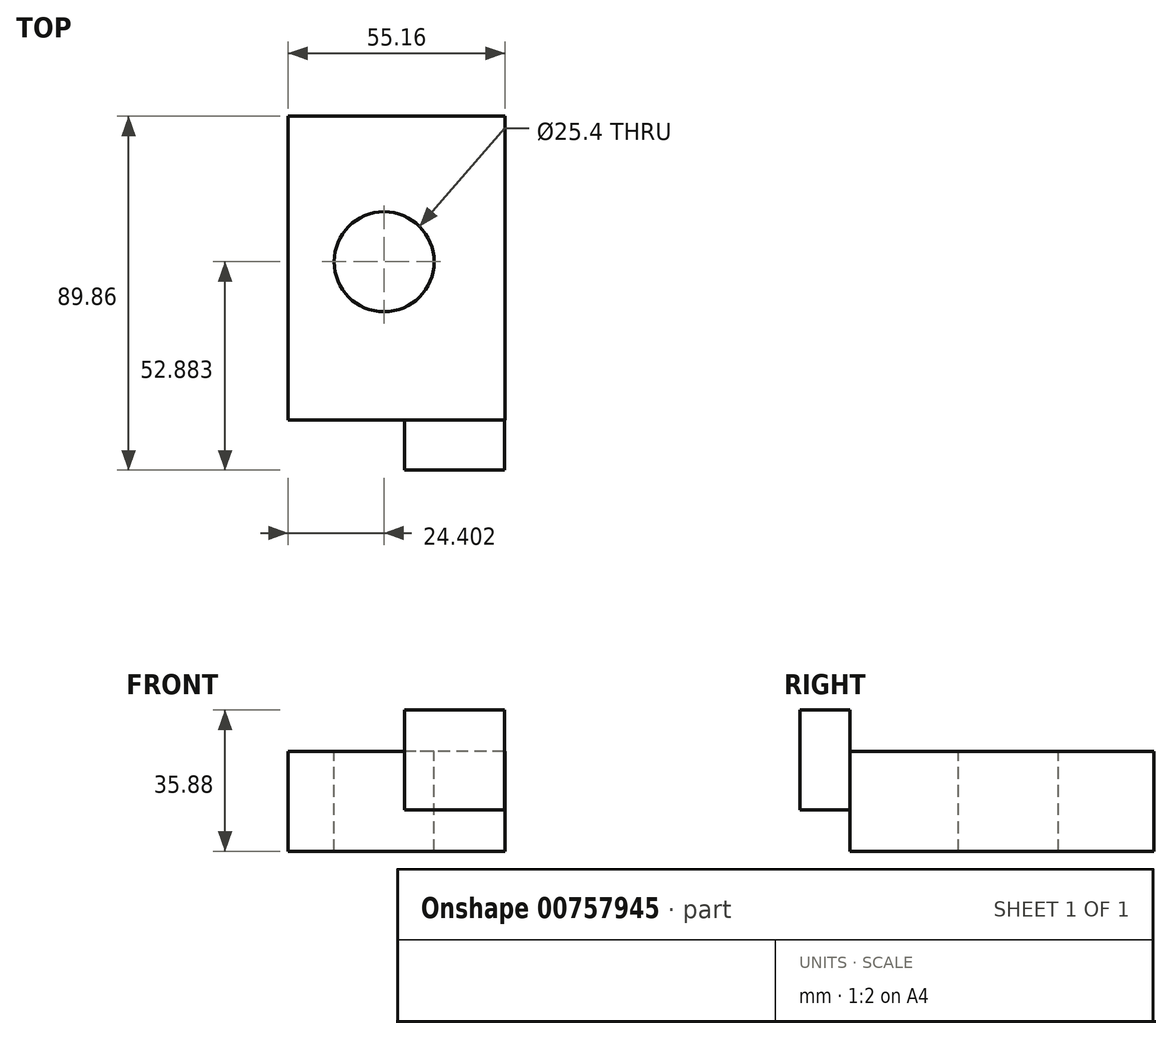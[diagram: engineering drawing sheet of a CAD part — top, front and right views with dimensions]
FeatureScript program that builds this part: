
annotation { "Feature Type Name" : "Feature", "Feature Type Description" : "" }
export const myFeature = defineFeature(function(context is Context, id is Id, definition is map)
    precondition{}
    {
        {
            var Q0;
            Q0=qCreatedBy(makeId("Top.planeOp"),FACE);
            var sketch = newSketch(context, id + "F0", { "sketchPlane" : qUnion([Q0])});
            skLineSegment(sketch, "E0.bottom", {"start": v(0, 0) * mm, "end": v(-55.16, 0) * mm});
            skLineSegment(sketch, "E0.top", {"start": v(0, 77.16) * mm, "end": v(-55.16, 77.16) * mm});
            skLineSegment(sketch, "E0.left", {"start": v(0, 0) * mm, "end": v(0, 77.16) * mm});
            skLineSegment(sketch, "E0.right", {"start": v(-55.16, 0) * mm, "end": v(-55.16, 77.16) * mm});
            skSolve(sketch);
        }
        {
            var Q0;
            Q0=makeQuery(id+"F0.imprint","IMPRINT",FACE,{"disambiguationData":[TD([[makeQuery(id+"F0.imprint","IMPRINT",EDGE,{"derivedFrom":sQuery(id+"F0.wireOp",EDGE,"E0.bottom")}),-1.0]])]});
            extrude(context, id + "F1", {"entities" : qUnion([Q0]), "depth" : 25.4 * mm, "offsetDistance" : 25.4 * mm});
        }
        {
            var Q0;
            Q0=makeQuery(id+"F1.opExtrude","CAP_FACE",FACE,{"disambiguationData":[OSD([sQuery(id+"F0.wireOp",EDGE,"E0.bottom"),sQuery(id+"F0.wireOp",EDGE,"E0.top"),sQuery(id+"F0.wireOp",EDGE,"E0.left"),sQuery(id+"F0.wireOp",EDGE,"E0.right")])],"isStart":false});
            var sketch = newSketch(context, id + "F2", { "sketchPlane" : qUnion([Q0])});
            skPoint(sketch, "E1", {"position": v(-30.76, 40.18) * mm});
            skSolve(sketch);
        }
        {
            var Q0;
            Q0=sQuery(id+"F2.wireOp",VERTEX,"E1");
            var Q1;
            Q1=makeQuery(id+"F1.opExtrude","SWEPT_BODY",BODY,{"disambiguationData":[OSD([sQuery(id+"F0.wireOp",EDGE,"E0.bottom"),sQuery(id+"F0.wireOp",EDGE,"E0.top"),sQuery(id+"F0.wireOp",EDGE,"E0.left"),sQuery(id+"F0.wireOp",EDGE,"E0.right")])]});
            hole(context, id + "F3", {"style" : HoleStyle.SIMPLE, "endStyle" : HoleEndStyle.THROUGH, "holeDiameter" : 25.4 * mm, "majorDiameter" : 6.35 * mm, "isTappedThrough" : true, "tappedDepth" : 12.7 * mm, "tapClearance" : 3, "locations" : qUnion([Q0]), "scope" : qUnion([Q1])});
        }
        {
            var Q0;
            Q0=makeQuery(id+"F1.opExtrude","SWEPT_FACE",FACE,{"disambiguationData":[OSD([sQuery(id+"F0.wireOp",EDGE,"E0.bottom")])]});
            var sketch = newSketch(context, id + "F4", { "sketchPlane" : qUnion([Q0])});
            skPoint(sketch, "E2", {"position": v(-17.06, 38.1) * mm});
            skPoint(sketch, "E3", {"position": v(-75.74, 38.1) * mm});
            skLineSegment(sketch, "E4.bottom", {"start": v(-25.6, 10.48) * mm, "end": v(-0.2, 10.48) * mm});
            skLineSegment(sketch, "E4.top", {"start": v(-25.6, 35.88) * mm, "end": v(-0.2, 35.88) * mm});
            skLineSegment(sketch, "E4.left", {"start": v(-25.6, 10.48) * mm, "end": v(-25.6, 35.88) * mm});
            skLineSegment(sketch, "E4.right", {"start": v(-0.2, 10.48) * mm, "end": v(-0.2, 35.88) * mm});
            skSolve(sketch);
        }
        {
            var Q0;
            Q0 = qSketchRegion(id + "F4", true);
            extrude(context, id + "F5", {"entities" : qUnion([Q0]), "operationType" : NewBodyOperationType.ADD, "depth" : 12.7 * mm, "offsetDistance" : 25.4 * mm});
        }
    });
